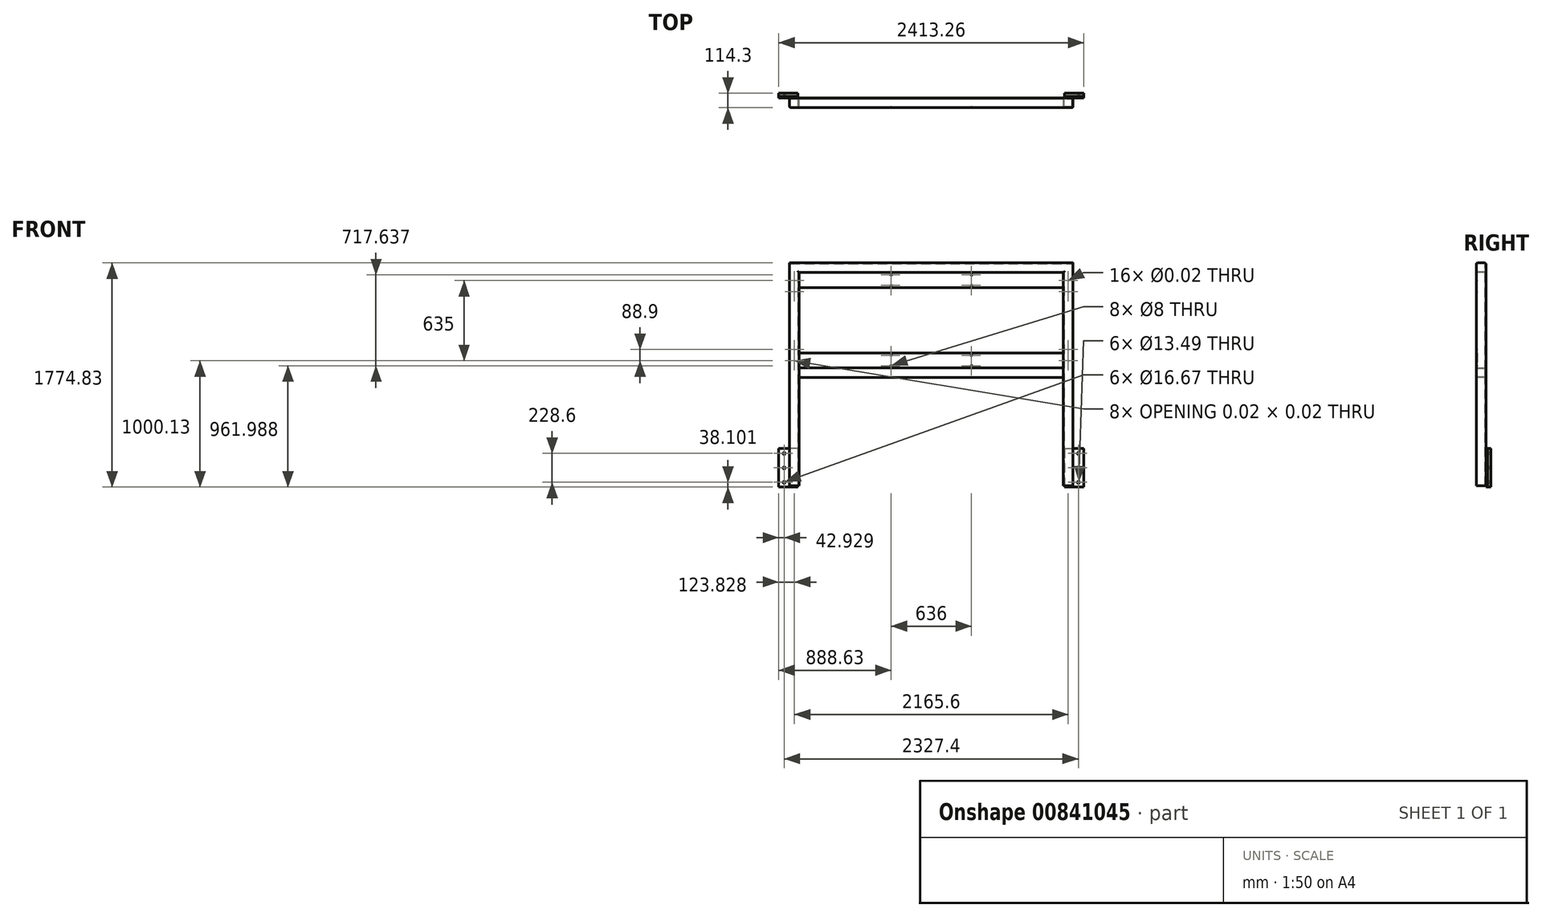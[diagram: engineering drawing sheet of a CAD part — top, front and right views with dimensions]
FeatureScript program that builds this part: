
annotation { "Feature Type Name" : "Feature", "Feature Type Description" : "" }
export const myFeature = defineFeature(function(context is Context, id is Id, definition is map)
    precondition{}
    {
        {
            var Q0;
            Q0=qCreatedBy(makeId("Front.planeOp"),FACE);
            var sketch = newSketch(context, id + "F0", { "sketchPlane" : qUnion([Q0])});
            skLineSegment(sketch, "E0", {"start": v(0, 176.4) * mm, "end": v(0, -211.24) * mm, "construction": true});
            skLineSegment(sketch, "E1.0", {"start": v(1044.58, 176.4) * mm, "end": v(1044.58, -211.24) * mm, "construction": true});
            skLineSegment(sketch, "E2", {"start": v(-190.83, 105.7) * mm, "end": v(1127.88, 105.7) * mm, "construction": true});
            skLineSegment(sketch, "E3.0", {"start": v(1054.23, 176.4) * mm, "end": v(1054.23, -211.24) * mm, "construction": true});
            skLineSegment(sketch, "E4.bottom", {"start": v(1054.23, 105.7) * mm, "end": v(1206.63, 105.7) * mm});
            skLineSegment(sketch, "E4.top", {"start": v(1054.23, -199.1) * mm, "end": v(1206.63, -199.1) * mm});
            skLineSegment(sketch, "E4.left", {"start": v(1054.23, 105.7) * mm, "end": v(1054.23, -199.1) * mm});
            skLineSegment(sketch, "E4.right", {"start": v(1206.63, 105.7) * mm, "end": v(1206.63, -199.1) * mm});
            skSolve(sketch);
        }
        {
            var Q0;
            Q0 = qSketchRegion(id + "F0", true);
            extrude(context, id + "F1", {"entities" : qUnion([Q0]), "oppositeDirection" : true, "depth" : 25.4 * mm, "offsetDistance" : 25.4 * mm});
        }
        {
            var Q0;
            Q0=makeQuery(id+"F1.opExtrude","CAP_FACE",FACE,{"disambiguationData":[OSD([sQuery(id+"F0.wireOp",EDGE,"E4.bottom"),sQuery(id+"F0.wireOp",EDGE,"E4.top"),sQuery(id+"F0.wireOp",EDGE,"E4.left"),sQuery(id+"F0.wireOp",EDGE,"E4.right")])],"isStart":true});
            var sketch = newSketch(context, id + "F2", { "sketchPlane" : qUnion([Q0])});
            skLineSegment(sketch, "E5.0", {"start": v(1054.23, 105.7) * mm, "end": v(1054.23, -199.1) * mm, "construction": true});
            skLineSegment(sketch, "E6.0", {"start": v(1044.58, 105.7) * mm, "end": v(1044.58, -199.1) * mm, "construction": true});
            skLineSegment(sketch, "E7.0", {"start": v(1120.78, 105.7) * mm, "end": v(1120.78, -199.1) * mm, "construction": true});
            skLineSegment(sketch, "E8", {"start": v(1206.63, -46.7) * mm, "end": v(1120.78, -46.7) * mm, "construction": true});
            skLineSegment(sketch, "E9", {"start": v(1163.7, -46.7) * mm, "end": v(1163.7, 67.6) * mm, "construction": true});
            skPoint(sketch, "E10", {"position": v(1163.7, 67.6) * mm});
            skPoint(sketch, "E11", {"position": v(1163.7, -46.7) * mm});
            skLineSegment(sketch, "E12.MirrorCS", {"start": v(1163.7, -46.7) * mm, "end": v(1163.7, -161) * mm, "construction": true});
            skPoint(sketch, "E13", {"position": v(1163.7, -161) * mm});
            skSolve(sketch);
        }
        {
            var Q0;
            Q0=sQuery(id+"F2.wireOp",VERTEX,"E10");
            var Q1;
            Q1=sQuery(id+"F2.wireOp",VERTEX,"E11");
            var Q2;
            Q2=sQuery(id+"F2.wireOp",VERTEX,"E12.MirrorCS.end");
            var Q3;
            Q3=makeQuery(id+"F1.opExtrude","SWEPT_BODY",BODY,{"disambiguationData":[OSD([sQuery(id+"F0.wireOp",EDGE,"E4.bottom"),sQuery(id+"F0.wireOp",EDGE,"E4.top"),sQuery(id+"F0.wireOp",EDGE,"E4.left"),sQuery(id+"F0.wireOp",EDGE,"E4.right")])]});
            hole(context, id + "F3", {"style" : HoleStyle.SIMPLE, "endStyle" : HoleEndStyle.THROUGH, "standardTappedOrClearance" : lookupTablePath({ "standard" : "ANSI", "engagement" : "75%", "pitch" : "11 tpi", "size" : "5/8", "type" : "Tapped" }), "standardBlindInLast" : lookupTablePath({ "standard" : "ANSI", "engagement" : "75%", "pitch" : "11 tpi", "size" : "5/8", "type" : "Tapped" }), "holeDiameter" : 13.5 * mm, "majorDiameter" : 15.88 * mm, "showTappedDepth" : true, "isTappedThrough" : true, "tappedDepth" : 38.1 * mm, "tapClearance" : 3, "startFromSketch" : true, "locations" : qUnion([Q0, Q1, Q2]), "scope" : qUnion([Q3])});
        }
        {
            var Q0;
            Q0=makeQuery(id+"F1.opExtrude","CAP_FACE",FACE,{"disambiguationData":[OSD([sQuery(id+"F0.wireOp",EDGE,"E4.bottom"),sQuery(id+"F0.wireOp",EDGE,"E4.top"),sQuery(id+"F0.wireOp",EDGE,"E4.left"),sQuery(id+"F0.wireOp",EDGE,"E4.right")])],"isStart":true});
            var sketch = newSketch(context, id + "F4", { "sketchPlane" : qUnion([Q0])});
            skLineSegment(sketch, "E14.0", {"start": v(1054.23, 105.7) * mm, "end": v(1054.23, -199.1) * mm});
            skLineSegment(sketch, "E14.1", {"start": v(1054.23, 105.7) * mm, "end": v(1206.63, 105.7) * mm});
            skLineSegment(sketch, "E14.2", {"start": v(1206.63, 105.7) * mm, "end": v(1206.63, -199.1) * mm});
            skLineSegment(sketch, "E14.3", {"start": v(1054.23, -199.1) * mm, "end": v(1206.63, -199.1) * mm});
            skCircle(sketch, "E15.0", {"center": v(1163.7, 67.6) * mm, "radius": 6.75 * mm, "construction": true});
            skCircle(sketch, "E16.0", {"center": v(1163.7, -46.7) * mm, "radius": 6.75 * mm, "construction": true});
            skCircle(sketch, "E17.0", {"center": v(1163.7, -161) * mm, "radius": 6.75 * mm, "construction": true});
            skSolve(sketch);
        }
        {
            var Q0;
            Q0 = qSketchRegion(id + "F4", true);
            extrude(context, id + "F5", {"entities" : qUnion([Q0]), "depth" : 12.7 * mm, "offsetDistance" : 25.4 * mm});
        }
        {
            var Q0;
            Q0=sQuery(id+"F4.wireOp",VERTEX,"E15.0.center");
            var Q1;
            Q1=sQuery(id+"F4.wireOp",VERTEX,"E16.0.center");
            var Q2;
            Q2=sQuery(id+"F4.wireOp",VERTEX,"E17.0.center");
            var Q3;
            Q3=makeQuery(id+"F5.opExtrude","SWEPT_BODY",BODY,{"disambiguationData":[OSD([sQuery(id+"F4.wireOp",EDGE,"E14.0"),sQuery(id+"F4.wireOp",EDGE,"E14.1"),sQuery(id+"F4.wireOp",EDGE,"E14.2"),sQuery(id+"F4.wireOp",EDGE,"E14.3")])]});
            hole(context, id + "F6", {"style" : HoleStyle.SIMPLE, "endStyle" : HoleEndStyle.THROUGH, "oppositeDirection" : true, "standardTappedOrClearance" : lookupTablePath({ "fit" : "Normal (ASME)", "standard" : "ANSI", "size" : "5/8", "type" : "Clearance" }), "standardBlindInLast" : lookupTablePath({ "fit" : "Free", "standard" : "ANSI", "size" : "5/8", "type" : "Clearance" }), "holeDiameter" : 16.67 * mm, "majorDiameter" : 15.88 * mm, "isTappedThrough" : true, "tappedDepth" : 38.1 * mm, "tapClearance" : 3, "startFromSketch" : true, "locations" : qUnion([Q0, Q1, Q2]), "scope" : qUnion([Q3])});
        }
        {
            var Q0;
            Q0=makeQuery(id+"F1.opExtrude","SWEPT_BODY",BODY,{"disambiguationData":[OSD([sQuery(id+"F0.wireOp",EDGE,"E4.bottom"),sQuery(id+"F0.wireOp",EDGE,"E4.top"),sQuery(id+"F0.wireOp",EDGE,"E4.left"),sQuery(id+"F0.wireOp",EDGE,"E4.right")])]});
            var Q1;
            Q1=makeQuery(id+"F5.opExtrude","SWEPT_BODY",BODY,{"disambiguationData":[OSD([sQuery(id+"F4.wireOp",EDGE,"E14.0"),sQuery(id+"F4.wireOp",EDGE,"E14.1"),sQuery(id+"F4.wireOp",EDGE,"E14.2"),sQuery(id+"F4.wireOp",EDGE,"E14.3")])]});
            var Q2;
            Q2=qCreatedBy(makeId("Right.planeOp"),FACE);
            mirror(context, id + "F7", {"entities" : qUnion([Q0, Q1]), "mirrorPlane" : qUnion([Q2])});
        }
        {
            var Q0;
            Q0=makeQuery(id+"F5.opExtrude","CAP_FACE",FACE,{"disambiguationData":[OSD([sQuery(id+"F4.wireOp",EDGE,"E14.0"),sQuery(id+"F4.wireOp",EDGE,"E14.1"),sQuery(id+"F4.wireOp",EDGE,"E14.2"),sQuery(id+"F4.wireOp",EDGE,"E14.3")])],"isStart":false});
            cPlane(context, id + "F8", {"entities" : qUnion([Q0]), "cplaneType" : CPlaneType.OFFSET, "offset" : 38.1 * mm, "width" : 152.4 * mm, "height" : 152.4 * mm});
        }
        {
            var Q0;
            Q0=qCreatedBy(id+"F8.planeOp",FACE);
            var sketch = newSketch(context, id + "F9", { "sketchPlane" : qUnion([Q0])});
            skLineSegment(sketch, "E18.0", {"start": v(1054.23, -199.1) * mm, "end": v(1206.63, -199.1) * mm, "construction": true});
            skLineSegment(sketch, "E19.0", {"start": v(1054.23, -189.58) * mm, "end": v(1206.63, -189.58) * mm, "construction": true});
            skLineSegment(sketch, "E20.0", {"start": v(1044.7, 105.7) * mm, "end": v(1044.7, -199.1) * mm, "construction": true});
            skLineSegment(sketch, "E21.0", {"start": v(1082.8, 1537.62) * mm, "end": v(1082.8, -189.58) * mm});
            skLineSegment(sketch, "E22", {"start": v(0, -389.47) * mm, "end": v(0, 403.65) * mm, "construction": true});
            skLineSegment(sketch, "E23.MirrorCS", {"start": v(-1082.8, 1537.62) * mm, "end": v(-1082.8, -189.58) * mm});
            skLineSegment(sketch, "E24", {"start": v(-1082.8, 1537.62) * mm, "end": v(1082.8, 1537.62) * mm});
            skSolve(sketch);
        }
        {
            var Q0;
            Q0=makeQuery(id+"F7.opPattern","COPY",FACE,{"derivedFrom":makeQuery(id+"F5.opExtrude","SWEPT_FACE",FACE,{"disambiguationData":[OSD([sQuery(id+"F4.wireOp",EDGE,"E14.3")])]}),"instanceName":"1"});
            cPlane(context, id + "F10", {"entities" : qUnion([Q0]), "cplaneType" : CPlaneType.OFFSET, "offset" : 9.52 * mm, "oppositeDirection" : true, "width" : 152.4 * mm, "height" : 152.4 * mm});
        }
        {
            var Q0;
            Q0=qCreatedBy(id+"F10.planeOp",FACE);
            var sketch = newSketch(context, id + "F11", { "sketchPlane" : qUnion([Q0])});
            skPoint(sketch, "E25.0", {"position": v(-1082.8, 50.8) * mm});
            skLineSegment(sketch, "E26.bottom", {"start": v(-1111.38, 88.9) * mm, "end": v(-1054.23, 88.9) * mm});
            skLineSegment(sketch, "E26.top", {"start": v(-1111.38, 12.7) * mm, "end": v(-1054.23, 12.7) * mm});
            skLineSegment(sketch, "E26.left", {"start": v(-1120.9, 79.37) * mm, "end": v(-1120.9, 22.22) * mm});
            skLineSegment(sketch, "E26.right", {"start": v(-1044.7, 79.37) * mm, "end": v(-1044.7, 22.22) * mm});
            skPoint(sketch, "E27.visualSharp", {"position": v(-1120.9, 88.9) * mm});
            skArc(sketch, "E27.filletArc", {"start": v(-1111.38, 88.9) * mm, "mid": v(-1118.11, 86.11) * mm, "end": v(-1120.9, 79.37) * mm});
            skPoint(sketch, "E28.visualSharp", {"position": v(-1044.7, 88.9) * mm});
            skArc(sketch, "E28.filletArc", {"start": v(-1044.7, 79.37) * mm, "mid": v(-1047.5, 86.11) * mm, "end": v(-1054.23, 88.9) * mm});
            skPoint(sketch, "E29.visualSharp", {"position": v(-1044.7, 12.7) * mm});
            skArc(sketch, "E29.filletArc", {"start": v(-1054.23, 12.7) * mm, "mid": v(-1047.5, 15.49) * mm, "end": v(-1044.7, 22.22) * mm});
            skPoint(sketch, "E30.visualSharp", {"position": v(-1120.9, 12.7) * mm});
            skArc(sketch, "E30.filletArc", {"start": v(-1120.9, 22.22) * mm, "mid": v(-1118.11, 15.49) * mm, "end": v(-1111.38, 12.7) * mm});
            skLineSegment(sketch, "E31.0", {"start": v(-1111.38, 82.55) * mm, "end": v(-1054.23, 82.55) * mm});
            skArc(sketch, "E31.1", {"start": v(-1051.05, 79.37) * mm, "mid": v(-1051.98, 81.62) * mm, "end": v(-1054.23, 82.55) * mm});
            skArc(sketch, "E31.2", {"start": v(-1111.38, 82.55) * mm, "mid": v(-1113.62, 81.62) * mm, "end": v(-1114.55, 79.37) * mm});
            skLineSegment(sketch, "E31.3", {"start": v(-1051.05, 79.37) * mm, "end": v(-1051.05, 22.22) * mm});
            skLineSegment(sketch, "E31.4", {"start": v(-1114.55, 79.37) * mm, "end": v(-1114.55, 22.22) * mm});
            skArc(sketch, "E31.5", {"start": v(-1114.55, 22.22) * mm, "mid": v(-1113.62, 19.98) * mm, "end": v(-1111.38, 19.05) * mm});
            skLineSegment(sketch, "E31.6", {"start": v(-1111.38, 19.05) * mm, "end": v(-1054.23, 19.05) * mm});
            skArc(sketch, "E31.7", {"start": v(-1054.23, 19.05) * mm, "mid": v(-1051.98, 19.98) * mm, "end": v(-1051.05, 22.22) * mm});
            skSolve(sketch);
        }
        {
            var Q0;
            Q0=makeQuery(id+"F11.imprint","IMPRINT",FACE,{"disambiguationData":[TD([[makeQuery(id+"F11.imprint","IMPRINT",EDGE,{"derivedFrom":sQuery(id+"F11.wireOp",EDGE,"E26.bottom")}),-1.0]])]});
            var Q1;
            Q1=sQuery(id+"F9.wireOp",EDGE,"E23.MirrorCS");
            var Q2;
            Q2=sQuery(id+"F9.wireOp",EDGE,"E24");
            var Q3;
            Q3=sQuery(id+"F9.wireOp",EDGE,"E21.0");
            sweep(context, id + "F12", {"profiles" : qUnion([Q0]), "path" : qUnion([Q1, Q2, Q3])});
        }
        {
            var Q0;
            Q0=makeQuery(id+"F1.opExtrude","SWEPT_FACE",FACE,{"disambiguationData":[OSD([sQuery(id+"F0.wireOp",EDGE,"E4.top")])]});
            cPlane(context, id + "F13", {"entities" : qUnion([Q0]), "cplaneType" : CPlaneType.OFFSET, "offset" : 1320.8 * mm, "oppositeDirection" : true, "width" : 152.4 * mm, "height" : 152.4 * mm});
        }
        {
            var Q0;
            Q0=qCreatedBy(id+"F13.planeOp",FACE);
            var sketch = newSketch(context, id + "F14", { "sketchPlane" : qUnion([Q0])});
            skLineSegment(sketch, "E32.0", {"start": v(-1044.7, 79.37) * mm, "end": v(-1044.7, 22.22) * mm, "construction": true});
            skSolve(sketch);
        }
        {
            var Q0;
            Q0=makeQuery(id+"F12.opSweep","SWEPT_FACE",FACE,{"disambiguationData":[OSD([sQuery(id+"F9.wireOp",EDGE,"E23.MirrorCS"),sQuery(id+"F11.wireOp",EDGE,"E26.right")])]});
            var sketch = newSketch(context, id + "F15", { "sketchPlane" : qUnion([Q0])});
            skLineSegment(sketch, "E33.0", {"start": v(-79.37, 1121.7) * mm, "end": v(-22.22, 1121.7) * mm, "construction": true});
            skLineSegment(sketch, "E34", {"start": v(-50.8, 743.88) * mm, "end": v(-50.8, 705.78) * mm, "construction": true});
            skLineSegment(sketch, "E35.bottom", {"start": v(-79.37, 743.88) * mm, "end": v(-22.22, 743.88) * mm});
            skLineSegment(sketch, "E35.top", {"start": v(-79.37, 667.68) * mm, "end": v(-22.22, 667.68) * mm});
            skLineSegment(sketch, "E35.left", {"start": v(-88.9, 734.35) * mm, "end": v(-88.9, 677.2) * mm});
            skLineSegment(sketch, "E35.right", {"start": v(-12.7, 734.35) * mm, "end": v(-12.7, 677.2) * mm});
            skPoint(sketch, "E35.middle", {"position": v(-50.8, 705.78) * mm});
            skPoint(sketch, "E36.visualSharp", {"position": v(-88.9, 743.88) * mm});
            skArc(sketch, "E36.filletArc", {"start": v(-79.37, 743.88) * mm, "mid": v(-86.11, 741.09) * mm, "end": v(-88.9, 734.35) * mm});
            skPoint(sketch, "E37.visualSharp", {"position": v(-12.7, 743.88) * mm});
            skArc(sketch, "E37.filletArc", {"start": v(-12.7, 734.35) * mm, "mid": v(-15.49, 741.09) * mm, "end": v(-22.22, 743.88) * mm});
            skPoint(sketch, "E38.visualSharp", {"position": v(-12.7, 667.68) * mm});
            skArc(sketch, "E38.filletArc", {"start": v(-22.22, 667.68) * mm, "mid": v(-15.49, 670.47) * mm, "end": v(-12.7, 677.2) * mm});
            skPoint(sketch, "E39.visualSharp", {"position": v(-88.9, 667.68) * mm});
            skArc(sketch, "E39.filletArc", {"start": v(-88.9, 677.2) * mm, "mid": v(-86.11, 670.47) * mm, "end": v(-79.37, 667.68) * mm});
            skArc(sketch, "E40.0", {"start": v(-79.37, 739.12) * mm, "mid": v(-82.74, 737.72) * mm, "end": v(-84.14, 734.35) * mm});
            skLineSegment(sketch, "E40.1", {"start": v(-84.14, 734.35) * mm, "end": v(-84.14, 677.2) * mm});
            skLineSegment(sketch, "E40.2", {"start": v(-79.37, 739.12) * mm, "end": v(-22.22, 739.12) * mm});
            skArc(sketch, "E40.3", {"start": v(-84.14, 677.2) * mm, "mid": v(-82.74, 673.84) * mm, "end": v(-79.37, 672.44) * mm});
            skArc(sketch, "E40.4", {"start": v(-17.46, 734.35) * mm, "mid": v(-18.86, 737.72) * mm, "end": v(-22.22, 739.12) * mm});
            skLineSegment(sketch, "E40.5", {"start": v(-17.46, 734.35) * mm, "end": v(-17.46, 677.2) * mm});
            skArc(sketch, "E40.6", {"start": v(-22.22, 672.44) * mm, "mid": v(-18.86, 673.84) * mm, "end": v(-17.46, 677.2) * mm});
            skLineSegment(sketch, "E40.7", {"start": v(-79.37, 672.44) * mm, "end": v(-22.22, 672.44) * mm});
            skSolve(sketch);
        }
        {
            var Q0;
            Q0=makeQuery(id+"F15.imprint","IMPRINT",FACE,{"disambiguationData":[TD([[makeQuery(id+"F15.imprint","IMPRINT",EDGE,{"derivedFrom":sQuery(id+"F15.wireOp",EDGE,"E35.left")}),1.0]])]});
            var Q1;
            {var subQ0=sQuery(id+"F15.wireOp",EDGE,"E35.bottom");Q1=makeQuery(id+"F15.imprint","IMPRINT",FACE,{"disambiguationData":[TD([[makeQuery(id+"F15.imprint","IMPRINT",EDGE,{"derivedFrom":subQ0}),-1.0]])]});}
            var Q2;
            Q2=makeQuery(id+"F15.imprint","IMPRINT",FACE,{"disambiguationData":[TD([[makeQuery(id+"F15.imprint","IMPRINT",EDGE,{"derivedFrom":sQuery(id+"F15.wireOp",EDGE,"E35.right")}),-1.0]])]});
            var Q3;
            {var subQ0=sQuery(id+"F15.wireOp",EDGE,"E35.top");Q3=makeQuery(id+"F15.imprint","IMPRINT",FACE,{"disambiguationData":[TD([[makeQuery(id+"F15.imprint","IMPRINT",EDGE,{"derivedFrom":subQ0}),1.0]])]});}
            var Q4;
            Q4=makeQuery(id+"F12.opSweep","SWEPT_FACE",FACE,{"disambiguationData":[OSD([sQuery(id+"F9.wireOp",EDGE,"E21.0"),sQuery(id+"F11.wireOp",EDGE,"E26.right")])]});
            extrude(context, id + "F16", {"entities" : qUnion([Q0, Q1, Q2, Q3]), "operationType" : NewBodyOperationType.ADD, "endBound" : BoundingType.UP_TO_SURFACE, "depth" : 25.4 * mm, "endBoundEntityFace" : qUnion([Q4]), "offsetDistance" : 25.4 * mm});
        }
        {
            var Q0;
            {var subQ2=sQuery(id+"F11.wireOp",EDGE,"E26.right");var subQ3=sQuery(id+"F9.wireOp",EDGE,"E21.0");Q0=makeQuery(id+"F16.boolean.opBoolean","SPLIT",FACE,{"disambiguationData":[TD([makeQuery(id+"F16.opExtrude","SWEPT_FACE",FACE,{"disambiguationData":[OSD([sQuery(id+"F15.wireOp",EDGE,"E35.bottom")])]})])],"derivedFrom":makeQuery(id+"F12.opSweep","SWEPT_FACE",FACE,{"disambiguationData":[OSD([subQ3,subQ2])]})});}
            var sketch = newSketch(context, id + "F17", { "sketchPlane" : qUnion([Q0])});
            skLineSegment(sketch, "E41.0.0", {"start": v(88.9, -189.58) * mm, "end": v(88.9, 1509.04) * mm, "construction": true});
            skLineSegment(sketch, "E41.0.2", {"start": v(88.9, 1509.04) * mm, "end": v(88.9, -189.58) * mm, "construction": true});
            skLineSegment(sketch, "E41.0.4", {"start": v(88.9, -189.58) * mm, "end": v(88.9, 1566.2) * mm, "construction": true});
            skLineSegment(sketch, "E42.0.1", {"start": v(22.22, 1499.52) * mm, "end": v(79.37, 1499.52) * mm, "construction": true});
            skLineSegment(sketch, "E42.0.3", {"start": v(88.9, 1499.52) * mm, "end": v(22.23, 1499.52) * mm, "construction": true});
            skLineSegment(sketch, "E43.0.0", {"start": v(88.9, 667.68) * mm, "end": v(22.22, 667.68) * mm, "construction": true});
            skLineSegment(sketch, "E43.0.1", {"start": v(22.22, 667.68) * mm, "end": v(22.22, -189.58) * mm, "construction": true});
            skLineSegment(sketch, "E43.0.2", {"start": v(22.22, -189.58) * mm, "end": v(79.37, -189.58) * mm, "construction": true});
            skLineSegment(sketch, "E43.0.3", {"start": v(79.37, -189.58) * mm, "end": v(79.37, 667.68) * mm, "construction": true});
            skPoint(sketch, "E44.orphan", {"position": v(79.38, 1499.52) * mm});
            skLineSegment(sketch, "E45.bottom", {"start": v(88.9, 1499.52) * mm, "end": v(82.9, 1499.52) * mm});
            skLineSegment(sketch, "E45.top", {"start": v(88.9, 1379.52) * mm, "end": v(82.9, 1379.52) * mm});
            skLineSegment(sketch, "E45.left", {"start": v(88.9, 1499.52) * mm, "end": v(88.9, 1379.52) * mm});
            skLineSegment(sketch, "E45.right", {"start": v(82.9, 1499.52) * mm, "end": v(82.9, 1379.52) * mm});
            skLineSegment(sketch, "E46.bottom", {"start": v(88.9, 667.68) * mm, "end": v(82.9, 667.68) * mm});
            skLineSegment(sketch, "E46.top", {"start": v(88.9, 863.88) * mm, "end": v(82.9, 863.88) * mm});
            skLineSegment(sketch, "E46.left", {"start": v(88.9, 743.88) * mm, "end": v(88.9, 863.88) * mm});
            skLineSegment(sketch, "E46.right", {"start": v(82.9, 743.88) * mm, "end": v(82.9, 863.88) * mm});
            skLineSegment(sketch, "E47.0.0", {"start": v(79.37, 743.88) * mm, "end": v(22.22, 743.88) * mm, "construction": true});
            skLineSegment(sketch, "E47.0.2", {"start": v(22.23, 743.88) * mm, "end": v(88.9, 743.88) * mm, "construction": true});
            skPoint(sketch, "E48.orphan", {"position": v(79.38, 743.88) * mm});
            skLineSegment(sketch, "E49", {"start": v(82.9, 743.88) * mm, "end": v(88.9, 743.88) * mm});
            skSolve(sketch);
        }
        {
            var Q0;
            Q0=makeQuery(id+"F17.imprint","IMPRINT",FACE,{"disambiguationData":[TD([[makeQuery(id+"F17.imprint","IMPRINT",EDGE,{"derivedFrom":sQuery(id+"F17.wireOp",EDGE,"E45.bottom")}),1.0]])]});
            var Q1;
            Q1=makeQuery(id+"F17.imprint","IMPRINT",FACE,{"disambiguationData":[TD([[makeQuery(id+"F17.imprint","IMPRINT",EDGE,{"derivedFrom":sQuery(id+"F17.wireOp",EDGE,"E46.top")}),1.0]])]});
            var Q2;
            {var subQ4=sQuery(id+"F15.wireOp",EDGE,"E35.bottom");var subQ5=sQuery(id+"F11.wireOp",EDGE,"E26.right");var subQ7=sQuery(id+"F9.wireOp",EDGE,"E23.MirrorCS");Q2=makeQuery(id+"F16.boolean.opBoolean","SPLIT",FACE,{"disambiguationData":[TD([makeQuery(id+"F16.opExtrude","SWEPT_FACE",FACE,{"disambiguationData":[OSD([subQ4])]})])],"derivedFrom":makeQuery(id+"F12.opSweep","SWEPT_FACE",FACE,{"disambiguationData":[OSD([subQ7,subQ5])]})});}
            extrude(context, id + "F18", {"entities" : qUnion([Q0, Q1]), "endBound" : BoundingType.UP_TO_SURFACE, "depth" : 25 * mm, "endBoundEntityFace" : qUnion([Q2]), "offsetDistance" : 25 * mm});
        }
        {
            var Q0;
            Q0=makeQuery(id+"F18.opExtrude","SWEPT_FACE",FACE,{"disambiguationData":[OSD([sQuery(id+"F17.wireOp",EDGE,"E45.left")])]});
            var sketch = newSketch(context, id + "F19", { "sketchPlane" : qUnion([Q0])});
            skLineSegment(sketch, "E50.0", {"start": v(-1044.7, 1480.52) * mm, "end": v(1044.7, 1480.52) * mm, "construction": true});
            skLineSegment(sketch, "E51.0", {"start": v(-1044.7, 1398.52) * mm, "end": v(1044.7, 1398.52) * mm, "construction": true});
            skLineSegment(sketch, "E52.0", {"start": v(-1044.7, 762.88) * mm, "end": v(1044.7, 762.88) * mm, "construction": true});
            skLineSegment(sketch, "E53.0", {"start": v(-1044.7, 844.88) * mm, "end": v(1044.7, 844.88) * mm, "construction": true});
            skLineSegment(sketch, "E54", {"start": v(0, 1849.68) * mm, "end": v(0, 324.82) * mm, "construction": true});
            skLineSegment(sketch, "E55.0", {"start": v(-318, 1849.68) * mm, "end": v(-318, 324.82) * mm, "construction": true});
            skLineSegment(sketch, "E56.MirrorCS", {"start": v(318, 1849.68) * mm, "end": v(318, 324.82) * mm, "construction": true});
            skPoint(sketch, "E57", {"position": v(-318, 1480.52) * mm});
            skPoint(sketch, "E58", {"position": v(-318, 1398.52) * mm});
            skPoint(sketch, "E59", {"position": v(318, 1398.52) * mm});
            skPoint(sketch, "E60", {"position": v(318, 1480.52) * mm});
            skPoint(sketch, "E61", {"position": v(-318, 844.88) * mm});
            skPoint(sketch, "E62", {"position": v(-318, 762.88) * mm});
            skPoint(sketch, "E63", {"position": v(318, 762.88) * mm});
            skPoint(sketch, "E64", {"position": v(318, 844.88) * mm});
            skSolve(sketch);
        }
        {
            var Q0;
            Q0=sQuery(id+"F19.wireOp",VERTEX,"E61");
            var Q1;
            Q1=sQuery(id+"F19.wireOp",VERTEX,"E62");
            var Q2;
            Q2=sQuery(id+"F19.wireOp",VERTEX,"E64");
            var Q3;
            Q3=sQuery(id+"F19.wireOp",VERTEX,"E63");
            var Q4;
            Q4=sQuery(id+"F19.wireOp",VERTEX,"E57");
            var Q5;
            Q5=sQuery(id+"F19.wireOp",VERTEX,"E58");
            var Q6;
            Q6=sQuery(id+"F19.wireOp",VERTEX,"E60");
            var Q7;
            Q7=sQuery(id+"F19.wireOp",VERTEX,"E59");
            var Q8;
            Q8=makeQuery(id+"F18.opExtrude","SWEPT_BODY",BODY,{"disambiguationData":[OSD([sQuery(id+"F17.wireOp",EDGE,"E46.top"),sQuery(id+"F17.wireOp",EDGE,"E46.left"),sQuery(id+"F17.wireOp",EDGE,"E46.right"),sQuery(id+"F17.wireOp",EDGE,"E49")])]});
            var Q9;
            Q9=makeQuery(id+"F18.opExtrude","SWEPT_BODY",BODY,{"disambiguationData":[OSD([sQuery(id+"F17.wireOp",EDGE,"E45.bottom"),sQuery(id+"F17.wireOp",EDGE,"E45.top"),sQuery(id+"F17.wireOp",EDGE,"E45.left"),sQuery(id+"F17.wireOp",EDGE,"E45.right")])]});
            hole(context, id + "F20", {"style" : HoleStyle.SIMPLE, "endStyle" : HoleEndStyle.THROUGH, "standardTappedOrClearance" : lookupTablePath({ "standard" : "ISO", "size" : "8", "type" : "Drilled" }), "standardBlindInLast" : lookupTablePath({ "standard" : "ISO", "size" : "8", "type" : "Drilled" }), "holeDiameter" : 8 * mm, "majorDiameter" : 5 * mm, "isTappedThrough" : true, "tappedDepth" : 24.75 * mm, "tapClearance" : 3, "startFromSketch" : true, "locations" : qUnion([Q0, Q1, Q2, Q3, Q4, Q5, Q6, Q7]), "scope" : qUnion([Q8, Q9])});
        }
        {
            var Q0;
            Q0=makeQuery(id+"F12.opSweep","SWEPT_FACE",FACE,{"disambiguationData":[OSD([sQuery(id+"F9.wireOp",EDGE,"E23.MirrorCS"),sQuery(id+"F11.wireOp",EDGE,"E26.bottom")])]});
            var sketch = newSketch(context, id + "F21", { "sketchPlane" : qUnion([Q0])});
            skLineSegment(sketch, "E65.0", {"start": v(-1111.38, -189.58) * mm, "end": v(-1054.23, -189.58) * mm, "construction": true});
            skLineSegment(sketch, "E66", {"start": v(-1082.8, -189.58) * mm, "end": v(-1082.8, 801.02) * mm, "construction": true});
            skLineSegment(sketch, "E67", {"start": v(-1082.8, 801.02) * mm, "end": v(-1082.8, 889.92) * mm, "construction": true});
            skLineSegment(sketch, "E68", {"start": v(-1082.8, 889.92) * mm, "end": v(-1082.8, 1347.12) * mm, "construction": true});
            skLineSegment(sketch, "E69", {"start": v(-1082.8, 1347.12) * mm, "end": v(-1082.8, 1436.02) * mm, "construction": true});
            skPoint(sketch, "E70", {"position": v(-1082.8, 1436.02) * mm});
            skPoint(sketch, "E71", {"position": v(-1082.8, 1347.12) * mm});
            skPoint(sketch, "E72", {"position": v(-1082.8, 889.92) * mm});
            skPoint(sketch, "E73", {"position": v(-1082.8, 801.02) * mm});
            skLineSegment(sketch, "E74", {"start": v(0, 1973.73) * mm, "end": v(0, 481.55) * mm, "construction": true});
            skPoint(sketch, "E75.MirrorP", {"position": v(1082.8, 1436.02) * mm});
            skPoint(sketch, "E76.MirrorP", {"position": v(1082.8, 1347.12) * mm});
            skPoint(sketch, "E77.MirrorP", {"position": v(1082.8, 889.92) * mm});
            skPoint(sketch, "E78.MirrorP", {"position": v(1082.8, 801.02) * mm});
            skSolve(sketch);
        }
        {
            var Q0;
            Q0=sQuery(id+"F21.wireOp",VERTEX,"E70");
            var Q1;
            Q1=sQuery(id+"F21.wireOp",VERTEX,"E71");
            var Q2;
            Q2=sQuery(id+"F21.wireOp",VERTEX,"E72");
            var Q3;
            Q3=sQuery(id+"F21.wireOp",VERTEX,"E73");
            var Q4;
            Q4=sQuery(id+"F21.wireOp",VERTEX,"E75.MirrorP");
            var Q5;
            Q5=sQuery(id+"F21.wireOp",VERTEX,"E76.MirrorP");
            var Q6;
            Q6=sQuery(id+"F21.wireOp",VERTEX,"E77.MirrorP");
            var Q7;
            Q7=sQuery(id+"F21.wireOp",VERTEX,"E78.MirrorP");
            var Q8;
            Q8=makeQuery(id+"F12.opSweep","SWEPT_BODY",BODY,{"disambiguationData":[OSD([sQuery(id+"F9.wireOp",EDGE,"E21.0"),sQuery(id+"F11.wireOp",EDGE,"E26.bottom"),sQuery(id+"F11.wireOp",EDGE,"E26.top"),sQuery(id+"F11.wireOp",EDGE,"E26.left"),sQuery(id+"F11.wireOp",EDGE,"E26.right"),sQuery(id+"F11.wireOp",EDGE,"E27.filletArc"),sQuery(id+"F11.wireOp",EDGE,"E28.filletArc"),sQuery(id+"F11.wireOp",EDGE,"E29.filletArc"),sQuery(id+"F11.wireOp",EDGE,"E30.filletArc"),sQuery(id+"F11.wireOp",EDGE,"E31.0"),sQuery(id+"F11.wireOp",EDGE,"E31.1"),sQuery(id+"F11.wireOp",EDGE,"E31.2"),sQuery(id+"F11.wireOp",EDGE,"E31.3"),sQuery(id+"F11.wireOp",EDGE,"E31.4"),sQuery(id+"F11.wireOp",EDGE,"E31.5"),sQuery(id+"F11.wireOp",EDGE,"E31.6"),sQuery(id+"F11.wireOp",EDGE,"E31.7")])]});
            hole(context, id + "F22", {"style" : HoleStyle.SIMPLE, "endStyle" : HoleEndStyle.THROUGH, "standardTappedOrClearance" : lookupTablePath({ "standard" : "ANSI", "size" : "9/16 (0.56)", "type" : "Drilled" }), "standardBlindInLast" : lookupTablePath({ "standard" : "ANSI", "size" : "9/16", "type" : "Drilled" }), "holeDiameter" : 9 / 406.4 * mm, "majorDiameter" : 6.35 * mm, "isTappedThrough" : true, "tappedDepth" : 38.1 * mm, "tapClearance" : 3, "startFromSketch" : true, "locations" : qUnion([Q0, Q1, Q2, Q3, Q4, Q5, Q6, Q7]), "scope" : qUnion([Q8])});
        }
    });
